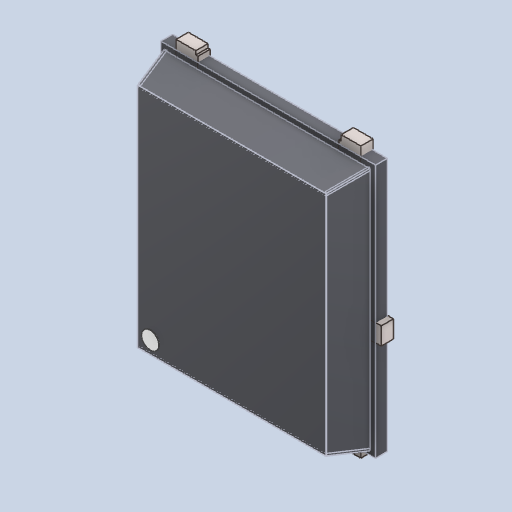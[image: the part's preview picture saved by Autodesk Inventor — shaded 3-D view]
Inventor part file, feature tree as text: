
AUTODESK INVENTOR PART (.ipt)
format: ipt  version: 2022 (Build 260153000, 153)  size: 188,928 bytes
history: native  units: mm
features: other x14, extrude x10
ambient origin geometry x8: Origin, YZ Plane, XZ Plane, XY Plane, X Axis, Y Axis, Z Axis, Center Point
bodies: Body1 (feature_tree), Body2 (feature_tree), Body3 (feature_tree), Body4 (feature_tree), Body5 (feature_tree), Body6 (feature_tree), Body7 (feature_tree), Body8 (feature_tree), Body9 (feature_tree), Body10 (feature_tree), Body11 (feature_tree), Body12 (feature_tree)
feature tree (24):
  other  "Твердое тело1"
  other  "Твердое тело2"
  other  "Твердое тело3"
  other  "Твердое тело4"
  other  "Твердое тело5"
  other  "Твердое тело6"
  other  "Твердое тело7"
  other  "Твердое тело8"
  other  "Твердое тело9"
  other  "Твердое тело10"
  other  "Твердое тело11"
  other  "Твердое тело12"
  extrude  "Extruded.STEP.STEP_21:1"  [1 undecoded]
  extrude  "Extruded_2.STEP.STEP_20:1"  [1 undecoded]
  extrude  "Extruded_2.STEP.STEP_20:2"  [1 undecoded]
  extrude  "Extruded.STEP.STEP_21:2"  [1 undecoded]
  other  "Cylinder.STEP.STEP_19:1"
  extrude  "Extruded_3.STEP.STEP_18:1"  [1 undecoded]
  extrude  "Extruded_4.STEP.STEP_17:1"  [1 undecoded]
  extrude  "Extruded_5.STEP.STEP_16:1"  [1 undecoded]
  extrude  "Extruded_5.STEP.STEP_16:2"  [1 undecoded]
  extrude  "Extruded_5.STEP.STEP_16:3"  [1 undecoded]
  extrude  "Extruded_5.STEP.STEP_16:4"  [1 undecoded]
  other  "Part9.STEP_3:1"
note: 10 required parameter values undecoded (feature->parameter linkage not recoverable at this tier; creation-order binding heuristic only, values carry confidence <= 0.55)
